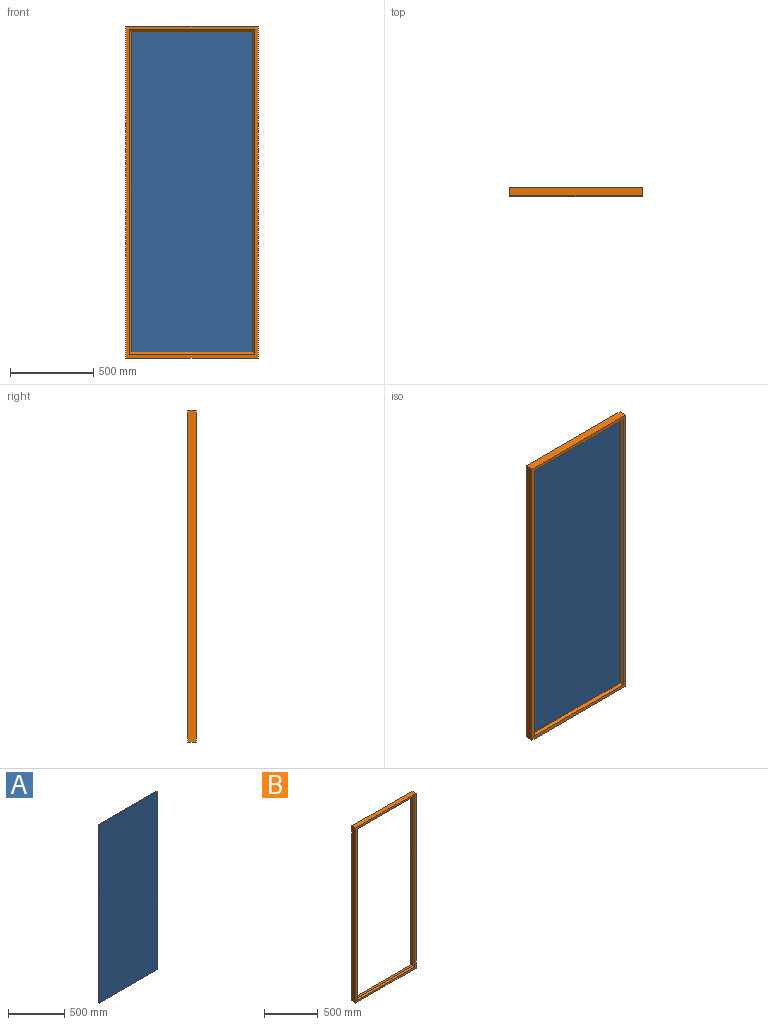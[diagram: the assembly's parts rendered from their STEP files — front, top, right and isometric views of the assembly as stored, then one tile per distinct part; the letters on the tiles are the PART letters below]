
ASSEMBLY  parts=2 mates=1
PART A: 6 faces, bbox 730x10x1930 mm
  f0: plane 1930x10mm, normal (1,0,0), area 19300mm2, adj f1,f3,f4,f5
  f1: plane 730x10mm, normal (0,0,1), area 7300mm2, adj f0,f2,f4,f5
  f2: plane 1930x10mm, normal (-1,0,0), area 19300mm2, adj f1,f3,f4,f5
  f3: plane 730x10mm, normal (0,0,-1), area 7300mm2, adj f0,f2,f4,f5
  f4: plane 1930x730mm, normal (0,-1,0), area 1408900mm2, adj f0,f1,f2,f3
  f5: plane 1930x730mm, normal (0,1,0), area 1408900mm2, adj f0,f1,f2,f3
PART B: 18 faces, bbox 800x50x2000 mm
  f0: plane 730x22mm, normal (0,0,-1), area 16060mm2, adj f1,f7,f13,f15
  f1: plane 1930x22mm, normal (-1,0,0), area 42460mm2, adj f0,f2,f11,f17
  f2: plane 730x22mm, normal (0,0,1), area 16060mm2, adj f1,f7,f10,f16
  f3: plane 2000x50mm, normal (1,0,0), area 100000mm2, adj f4,f6,f8,f9
  f4: plane 800x50mm, normal (0,0,1), area 40000mm2, adj f3,f5,f8,f9
  f5: plane 2000x50mm, normal (-1,0,0), area 100000mm2, adj f4,f6,f8,f9
  f6: plane 800x50mm, normal (0,0,-1), area 40000mm2, adj f3,f5,f8,f9
  f7: plane 1930x22mm, normal (1,0,0), area 42460mm2, adj f0,f2,f12,f14
  f8: plane 2000x800mm, normal (0,-1,0), area 115836mm2, adj f3,f4,f5,f6,f14,f15,f16,f17
  f9: plane 2000x800mm, normal (0,1,0), area 115836mm2, adj f3,f4,f5,f6,f10,f11,f12,f13
  f10: plane 758x14mm, normal (0,0.71,0.71), area 14730.4mm2, adj f2,f9,f11,f12
  f11: plane 1958x14mm, normal (-0.71,0.71,0), area 38489.2mm2, adj f1,f9,f10,f13
  f12: plane 1958x14mm, normal (0.71,0.71,0), area 38489.2mm2, adj f7,f9,f10,f13
  f13: plane 758x14mm, normal (0,0.71,-0.71), area 14730.4mm2, adj f0,f9,f11,f12
  f14: plane 1958x14mm, normal (0.71,-0.71,0), area 38489.2mm2, adj f7,f8,f15,f16
  f15: plane 758x14mm, normal (0,-0.71,-0.71), area 14730.4mm2, adj f0,f8,f14,f17
  f16: plane 758x14mm, normal (0,-0.71,0.71), area 14730.4mm2, adj f2,f8,f14,f17
  f17: plane 1958x14mm, normal (-0.71,-0.71,0), area 38489.2mm2, adj f1,f8,f15,f16
PLACE A t=(-219.46,54.75,264.68)mm
PLACE B t=(-219.46,74.75,264.68)mm
MATE fastened A.f3 <-> B.f2  axis (0,0,-1) through (-584.46,49.75,-700.32)mm
